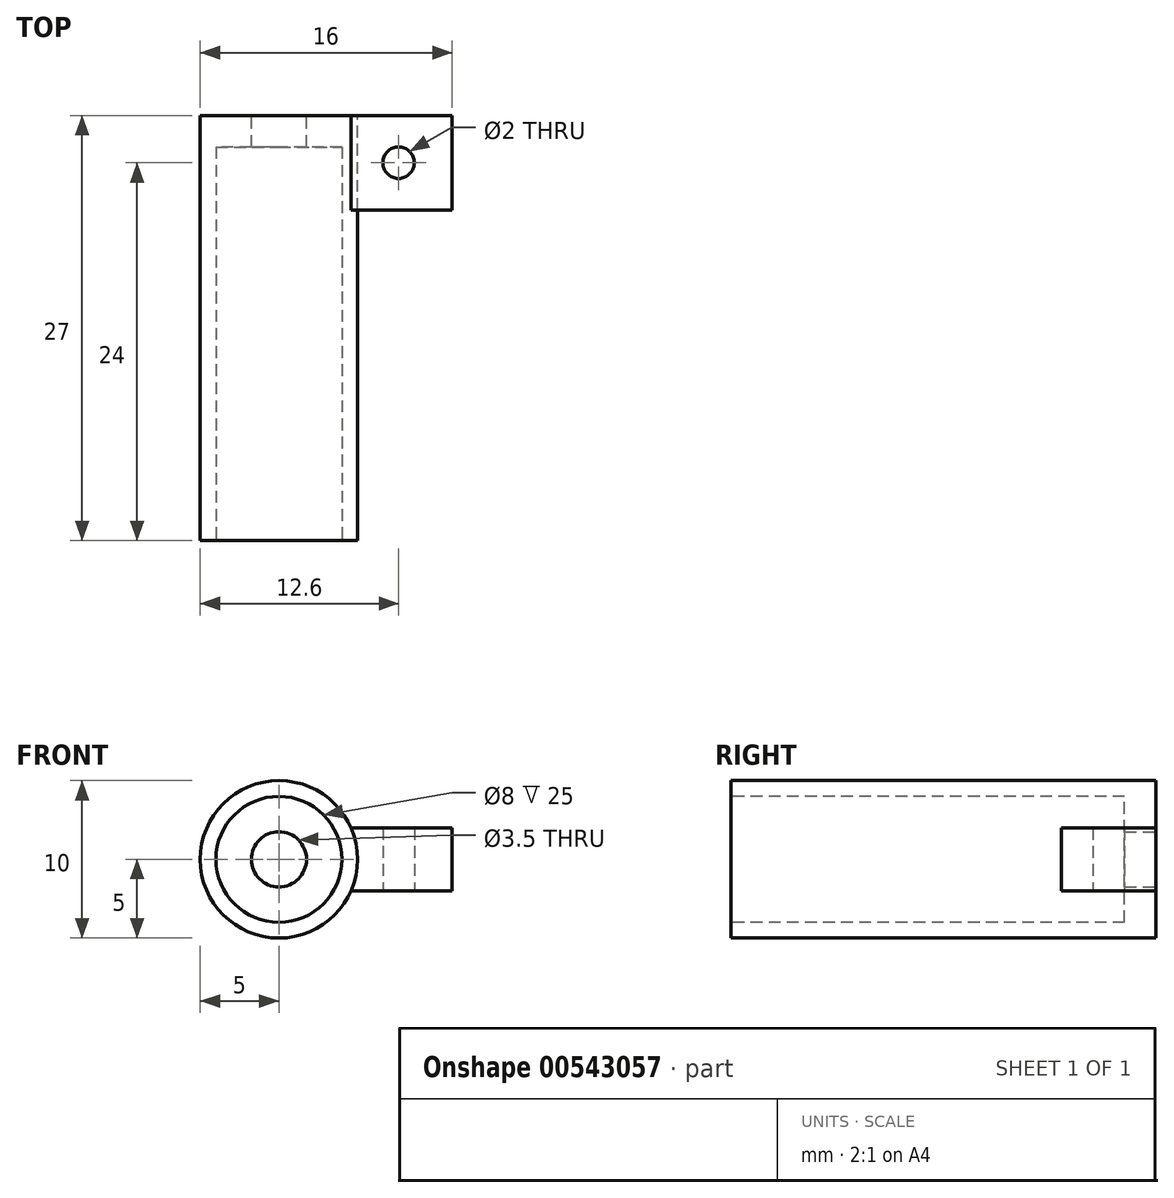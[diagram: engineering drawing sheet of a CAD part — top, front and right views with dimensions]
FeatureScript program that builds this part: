
annotation { "Feature Type Name" : "Feature", "Feature Type Description" : "" }
export const myFeature = defineFeature(function(context is Context, id is Id, definition is map)
    precondition{}
    {
        {
            var Q0;
            Q0=qCreatedBy(makeId("Front.planeOp"),FACE);
            var sketch = newSketch(context, id + "F0", { "sketchPlane" : qUnion([Q0])});
            skCircle(sketch, "E0", {"center": v(0, 0) * mm, "radius": 5 * mm});
            skSolve(sketch);
        }
        {
            var Q0;
            Q0=makeQuery(id+"F0.imprint","IMPRINT",FACE,{"disambiguationData":[TD([[makeQuery(id+"F0.imprint","IMPRINT",EDGE,{"derivedFrom":sQuery(id+"F0.wireOp",EDGE,"E0")}),1.0]])]});
            extrude(context, id + "F1", {"entities" : qUnion([Q0]), "depth" : 27 * mm, "offsetDistance" : 25 * mm});
        }
        {
            var Q0;
            Q0=makeQuery(id+"F1.opExtrude","CAP_FACE",FACE,{"disambiguationData":[OSD([sQuery(id+"F0.wireOp",EDGE,"E0")])],"isStart":false});
            var sketch = newSketch(context, id + "F2", { "sketchPlane" : qUnion([Q0])});
            skCircle(sketch, "E1", {"center": v(0, 0) * mm, "radius": 4 * mm});
            skSolve(sketch);
        }
        {
            var Q0;
            Q0=makeQuery(id+"F2.imprint","IMPRINT",FACE,{"disambiguationData":[TD([[makeQuery(id+"F2.imprint","IMPRINT",EDGE,{"derivedFrom":sQuery(id+"F2.wireOp",EDGE,"E1")}),1.0]])]});
            extrude(context, id + "F3", {"entities" : qUnion([Q0]), "operationType" : NewBodyOperationType.REMOVE, "oppositeDirection" : true, "depth" : 25 * mm, "offsetDistance" : 25 * mm});
        }
        {
            var Q0;
            Q0=makeQuery(id+"F1.opExtrude","CAP_FACE",FACE,{"disambiguationData":[OSD([sQuery(id+"F0.wireOp",EDGE,"E0")])],"isStart":true});
            var sketch = newSketch(context, id + "F4", { "sketchPlane" : qUnion([Q0])});
            skCircle(sketch, "E2", {"center": v(0, 0) * mm, "radius": 1.75 * mm});
            skSolve(sketch);
        }
        {
            var Q0;
            Q0=makeQuery(id+"F4.imprint","IMPRINT",FACE,{"disambiguationData":[TD([[makeQuery(id+"F4.imprint","IMPRINT",EDGE,{"derivedFrom":sQuery(id+"F4.wireOp",EDGE,"E2")}),1.0]])]});
            extrude(context, id + "F5", {"entities" : qUnion([Q0]), "operationType" : NewBodyOperationType.REMOVE, "oppositeDirection" : true, "depth" : 25 * mm, "offsetDistance" : 25 * mm});
        }
        {
            var Q0;
            Q0=makeQuery(id+"F1.opExtrude","CAP_FACE",FACE,{"disambiguationData":[OSD([sQuery(id+"F0.wireOp",EDGE,"E0")])],"isStart":true});
            var sketch = newSketch(context, id + "F6", { "sketchPlane" : qUnion([Q0])});
            skLineSegment(sketch, "E3", {"start": v(-4.58, -2) * mm, "end": v(-11, -2) * mm});
            skLineSegment(sketch, "E4", {"start": v(-11, -2) * mm, "end": v(-11, 2) * mm});
            skLineSegment(sketch, "E5", {"start": v(-11, 2) * mm, "end": v(-4.58, 2) * mm});
            skSolve(sketch);
        }
        {
            var Q0;
            {var subQ0=sQuery(id+"F6.wireOp",EDGE,"E3");Q0=makeQuery(id+"F6.imprint","IMPRINT",FACE,{"disambiguationData":[TD([[makeQuery(id+"F6.imprint","IMPRINT",EDGE,{"derivedFrom":subQ0}),-1.0]])]});}
            extrude(context, id + "F7", {"entities" : qUnion([Q0]), "oppositeDirection" : true, "depth" : 6 * mm, "offsetDistance" : 25 * mm});
        }
        {
            var Q0;
            Q0=makeQuery(id+"F7.opExtrude","SWEPT_FACE",FACE,{"disambiguationData":[OSD([sQuery(id+"F6.wireOp",EDGE,"E3")])]});
            var sketch = newSketch(context, id + "F8", { "sketchPlane" : qUnion([Q0])});
            skCircle(sketch, "E6", {"center": v(7.6, 3) * mm, "radius": 1 * mm});
            skSolve(sketch);
        }
        {
            var Q0;
            Q0=makeQuery(id+"F8.imprint","IMPRINT",FACE,{"disambiguationData":[TD([[makeQuery(id+"F8.imprint","IMPRINT",EDGE,{"derivedFrom":sQuery(id+"F8.wireOp",EDGE,"E6")}),1.0]])]});
            extrude(context, id + "F9", {"entities" : qUnion([Q0]), "operationType" : NewBodyOperationType.REMOVE, "oppositeDirection" : true, "depth" : 25 * mm, "offsetDistance" : 25 * mm});
        }
    });
